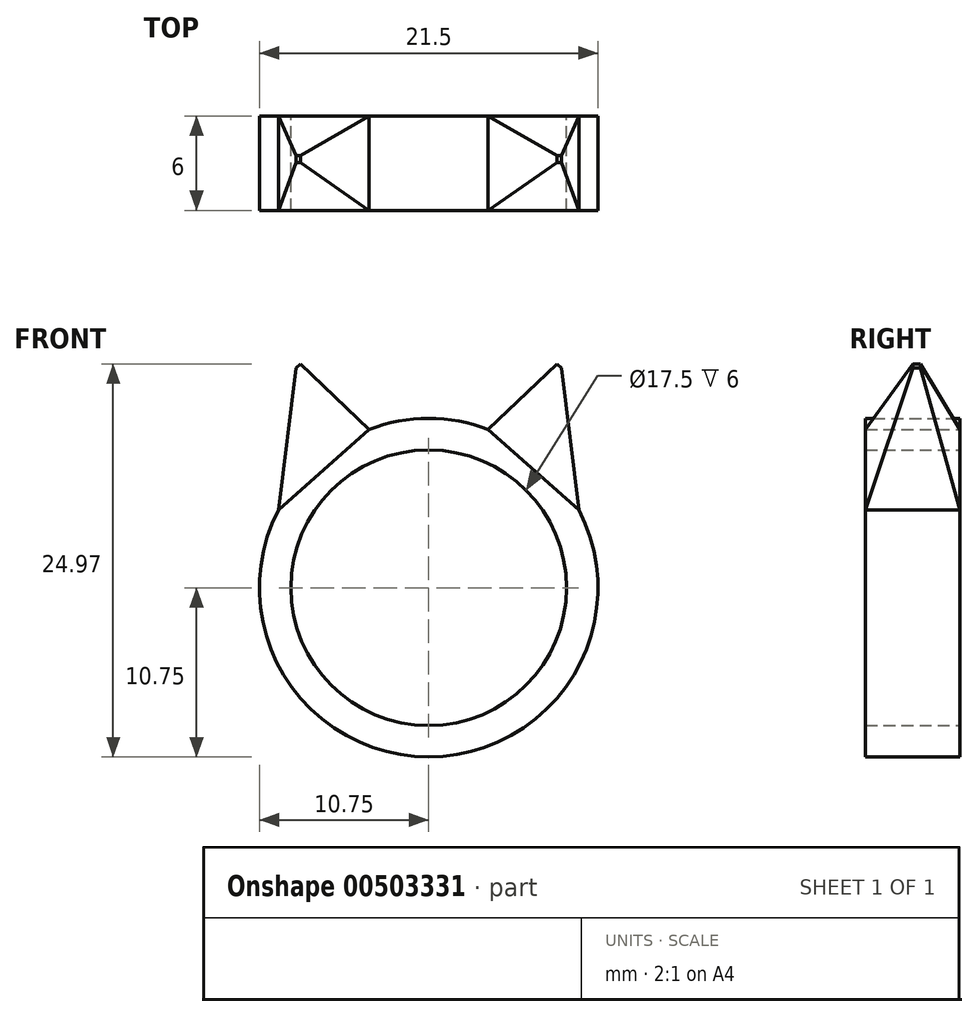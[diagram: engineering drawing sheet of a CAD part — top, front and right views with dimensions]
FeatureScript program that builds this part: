
annotation { "Feature Type Name" : "Feature", "Feature Type Description" : "" }
export const myFeature = defineFeature(function(context is Context, id is Id, definition is map)
    precondition{}
    {
        {
            var Q0;
            Q0=qCreatedBy(makeId("Front.planeOp"),FACE);
            var sketch = newSketch(context, id + "F0", { "sketchPlane" : qUnion([Q0])});
            skCircle(sketch, "E0", {"center": v(0, 0) * mm, "radius": 8.75 * mm});
            skArc(sketch, "E1", {"start": v(-9.54, 4.95) * mm, "mid": v(0, -10.75) * mm, "end": v(9.54, 4.95) * mm});
            skLineSegment(sketch, "E2", {"start": v(0, 0) * mm, "end": v(0, 20.24) * mm});
            skLineSegment(sketch, "E3", {"start": v(3.78, 10.06) * mm, "end": v(9.54, 4.95) * mm});
            skLineSegment(sketch, "E4.MirrorCS", {"start": v(-3.78, 10.06) * mm, "end": v(-9.54, 4.95) * mm});
            skArc(sketch, "E5.trimOffspring", {"start": v(3.78, 10.06) * mm, "mid": v(0, 10.75) * mm, "end": v(-3.78, 10.06) * mm});
            skSolve(sketch);
        }
        {
            var Q0;
            Q0=makeQuery(id+"F0.imprint","IMPRINT",FACE,{"disambiguationData":[TD([[makeQuery(id+"F0.imprint","IMPRINT",EDGE,{"derivedFrom":sQuery(id+"F0.wireOp",EDGE,"E0")}),-1.0]])]});
            extrude(context, id + "F1", {"entities" : qUnion([Q0]), "depth" : 6 * mm});
        }
        {
            var Q0;
            Q0=makeQuery(id+"F1.opExtrude","SWEPT_FACE",FACE,{"disambiguationData":[OSD([sQuery(id+"F0.wireOp",EDGE,"E3")])]});
            cPlane(context, id + "F2", {"entities" : qUnion([Q0]), "cplaneType" : CPlaneType.OFFSET, "offset" : 6 * mm, "width" : 152.4 * mm, "height" : 152.4 * mm});
        }
        {
            var Q0;
            Q0=qCreatedBy(id+"F2.planeOp",FACE);
            var sketch = newSketch(context, id + "F3", { "sketchPlane" : qUnion([Q0])});
            skLineSegment(sketch, "E6.bottom", {"start": v(-3.35, -2.52) * mm, "end": v(-2.95, -2.52) * mm});
            skLineSegment(sketch, "E6.top", {"start": v(-3.35, -2.97) * mm, "end": v(-2.95, -2.97) * mm});
            skLineSegment(sketch, "E6.left", {"start": v(-3.35, -2.52) * mm, "end": v(-3.35, -2.97) * mm});
            skLineSegment(sketch, "E6.right", {"start": v(-2.95, -2.52) * mm, "end": v(-2.95, -2.97) * mm});
            skSolve(sketch);
        }
        {
            var Q1;
            Q1=makeQuery(id+"F1.opExtrude","SWEPT_FACE",FACE,{"disambiguationData":[OSD([sQuery(id+"F0.wireOp",EDGE,"E3")])]});
            var Q2;
            Q2=makeQuery(id+"F3.imprint","IMPRINT",FACE,{"disambiguationData":[TD([[makeQuery(id+"F3.imprint","IMPRINT",EDGE,{"derivedFrom":sQuery(id+"F3.wireOp",EDGE,"E6.bottom")}),-1.0]])]});
            loft(context, id + "F4", {"operationType" : NewBodyOperationType.ADD, "sheetProfilesArray" : [{ "sheetProfileEntities" : qUnion([Q1]) }, { "sheetProfileEntities" : qUnion([Q2]) }]});
        }
        {
            var Q0;
            Q0=makeQuery(id+"F1.opExtrude","SWEPT_BODY",BODY,{"disambiguationData":[OSD([sQuery(id+"F0.wireOp",EDGE,"E0"),sQuery(id+"F0.wireOp",EDGE,"E1"),sQuery(id+"F0.wireOp",EDGE,"E3"),sQuery(id+"F0.wireOp",EDGE,"E4.MirrorCS"),sQuery(id+"F0.wireOp",EDGE,"E5.trimOffspring")])]});
            var Q1;
            Q1=qCreatedBy(makeId("Right.planeOp"),FACE);
            mirror(context, id + "F5", {"operationType" : NewBodyOperationType.ADD, "entities" : qUnion([Q0]), "mirrorPlane" : qUnion([Q1])});
        }
    });
